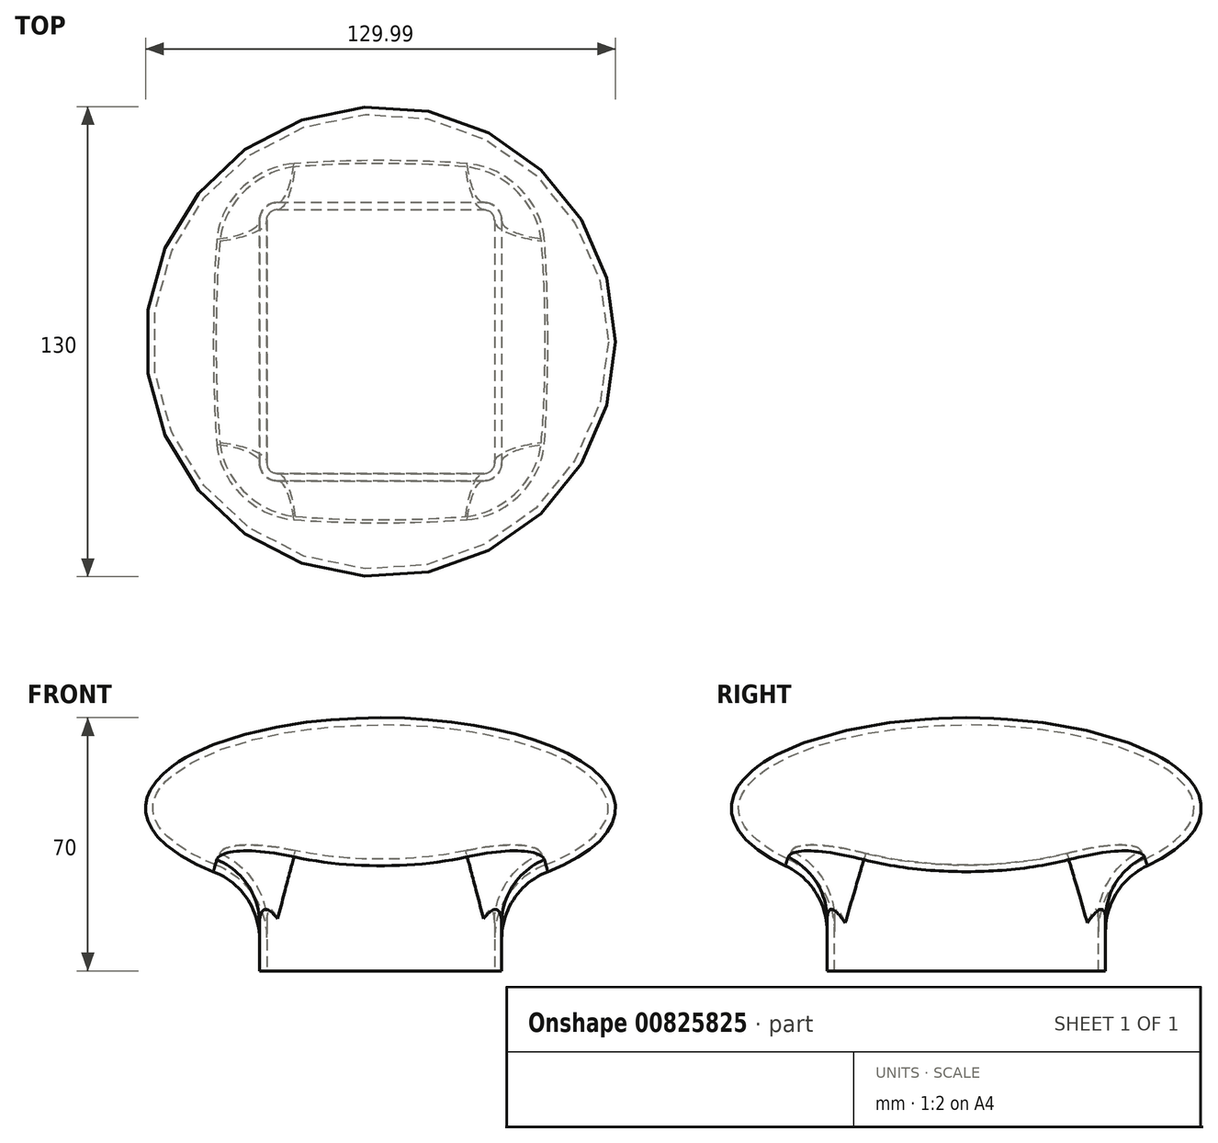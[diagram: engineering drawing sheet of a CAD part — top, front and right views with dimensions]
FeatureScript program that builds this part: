
annotation { "Feature Type Name" : "Feature", "Feature Type Description" : "" }
export const myFeature = defineFeature(function(context is Context, id is Id, definition is map)
    precondition{}
    {
        {
            var Q0;
            Q0=qCreatedBy(makeId("Top.planeOp"),FACE);
            var sketch = newSketch(context, id + "F0", { "sketchPlane" : qUnion([Q0])});
            skLineSegment(sketch, "E0.bottom", {"start": v(-33.5, 38.5) * mm, "end": v(33.5, 38.5) * mm});
            skLineSegment(sketch, "E0.top", {"start": v(-33.5, -38.5) * mm, "end": v(33.5, -38.5) * mm});
            skLineSegment(sketch, "E0.left", {"start": v(-33.5, 38.5) * mm, "end": v(-33.5, -38.5) * mm});
            skLineSegment(sketch, "E0.right", {"start": v(33.5, 38.5) * mm, "end": v(33.5, -38.5) * mm});
            skSolve(sketch);
        }
        {
            var Q0;
            Q0=makeQuery(id+"F0.imprint","IMPRINT",FACE,{"disambiguationData":[TD([[makeQuery(id+"F0.imprint","IMPRINT",EDGE,{"derivedFrom":sQuery(id+"F0.wireOp",EDGE,"E0.bottom")}),-1.0]])]});
            extrude(context, id + "F1", {"entities" : qUnion([Q0]), "depth" : 50 * mm, "offsetDistance" : 25 * mm});
        }
        {
            var Q0;
            Q0=qCreatedBy(makeId("Front.planeOp"),FACE);
            var sketch = newSketch(context, id + "F2", { "sketchPlane" : qUnion([Q0])});
            skEllipse(sketch, "E1", {"center": v(0, 45) * mm, "majorRadius": 65 * mm, "minorRadius": 25 * mm, "majorAxis": v(1, 0)});
            skLineSegment(sketch, "E2", {"start": v(0, 20) * mm, "end": v(0, 70) * mm});
            skSolve(sketch);
        }
        {
            var Q0;
            {var subQ0=sQuery(id+"F2.wireOp",EDGE,"E2");Q0=makeQuery(id+"F2.imprint","IMPRINT",FACE,{"disambiguationData":[TD([[makeQuery(id+"F2.imprint","IMPRINT",EDGE,{"derivedFrom":subQ0}),-1.0]])]});}
            var Q1;
            Q1=sQuery(id+"F2.wireOp",EDGE,"E2");
            revolve(context, id + "F3", {"operationType" : NewBodyOperationType.ADD, "surfaceOperationType" : NewSurfaceOperationType.NEW, "entities" : qUnion([Q0]), "axis" : qUnion([Q1]), "revolveType" : RevolveType.FULL});
        }
        {
            var Q0;
            Q0=makeQuery(id+"F1.opExtrude","SWEPT_EDGE",EDGE,{"disambiguationData":[OSD([sQuery(id+"F0.wireOp",EDGE,"E0.bottom"),sQuery(id+"F0.wireOp",EDGE,"E0.left")])]});
            var Q1;
            Q1=makeQuery(id+"F1.opExtrude","SWEPT_EDGE",EDGE,{"disambiguationData":[OSD([sQuery(id+"F0.wireOp",EDGE,"E0.bottom"),sQuery(id+"F0.wireOp",EDGE,"E0.right")])]});
            var Q2;
            Q2=makeQuery(id+"F1.opExtrude","SWEPT_EDGE",EDGE,{"disambiguationData":[OSD([sQuery(id+"F0.wireOp",EDGE,"E0.top"),sQuery(id+"F0.wireOp",EDGE,"E0.left")])]});
            var Q3;
            Q3=makeQuery(id+"F1.opExtrude","SWEPT_EDGE",EDGE,{"disambiguationData":[OSD([sQuery(id+"F0.wireOp",EDGE,"E0.top"),sQuery(id+"F0.wireOp",EDGE,"E0.right")])]});
            fillet(context, id + "F4", {"entities" : qUnion([Q0, Q1, Q2, Q3]), "radius" : 5 * mm, "tangentPropagation" : true, "allowEdgeOverflow" : false});
        }
        {
            var Q0;
            Q0=makeQuery(id+"F3.boolean.opBoolean","INTERSECT",EDGE,{"derivedFrom":[makeQuery(id+"F1.opExtrude","SWEPT_FACE",FACE,{"disambiguationData":[OSD([sQuery(id+"F0.wireOp",EDGE,"E0.top")])]}),makeQuery(id+"F3.opRevolve","SWEPT_FACE",FACE,{"disambiguationData":[OSD([sQuery(id+"F2.wireOp",EDGE,"E1")])]})]});
            fillet(context, id + "F5", {"entities" : qUnion([Q0]), "radius" : 20 * mm, "tangentPropagation" : true, "allowEdgeOverflow" : false});
        }
        {
            var Q0;
            Q0=makeQuery(id+"F1.opExtrude","CAP_FACE",FACE,{"disambiguationData":[OSD([sQuery(id+"F0.wireOp",EDGE,"E0.bottom"),sQuery(id+"F0.wireOp",EDGE,"E0.top"),sQuery(id+"F0.wireOp",EDGE,"E0.left"),sQuery(id+"F0.wireOp",EDGE,"E0.right")])],"isStart":true});
            shell(context, id + "F6", {"entities" : qUnion([Q0]), "thickness" : 2 * mm});
        }
    });
